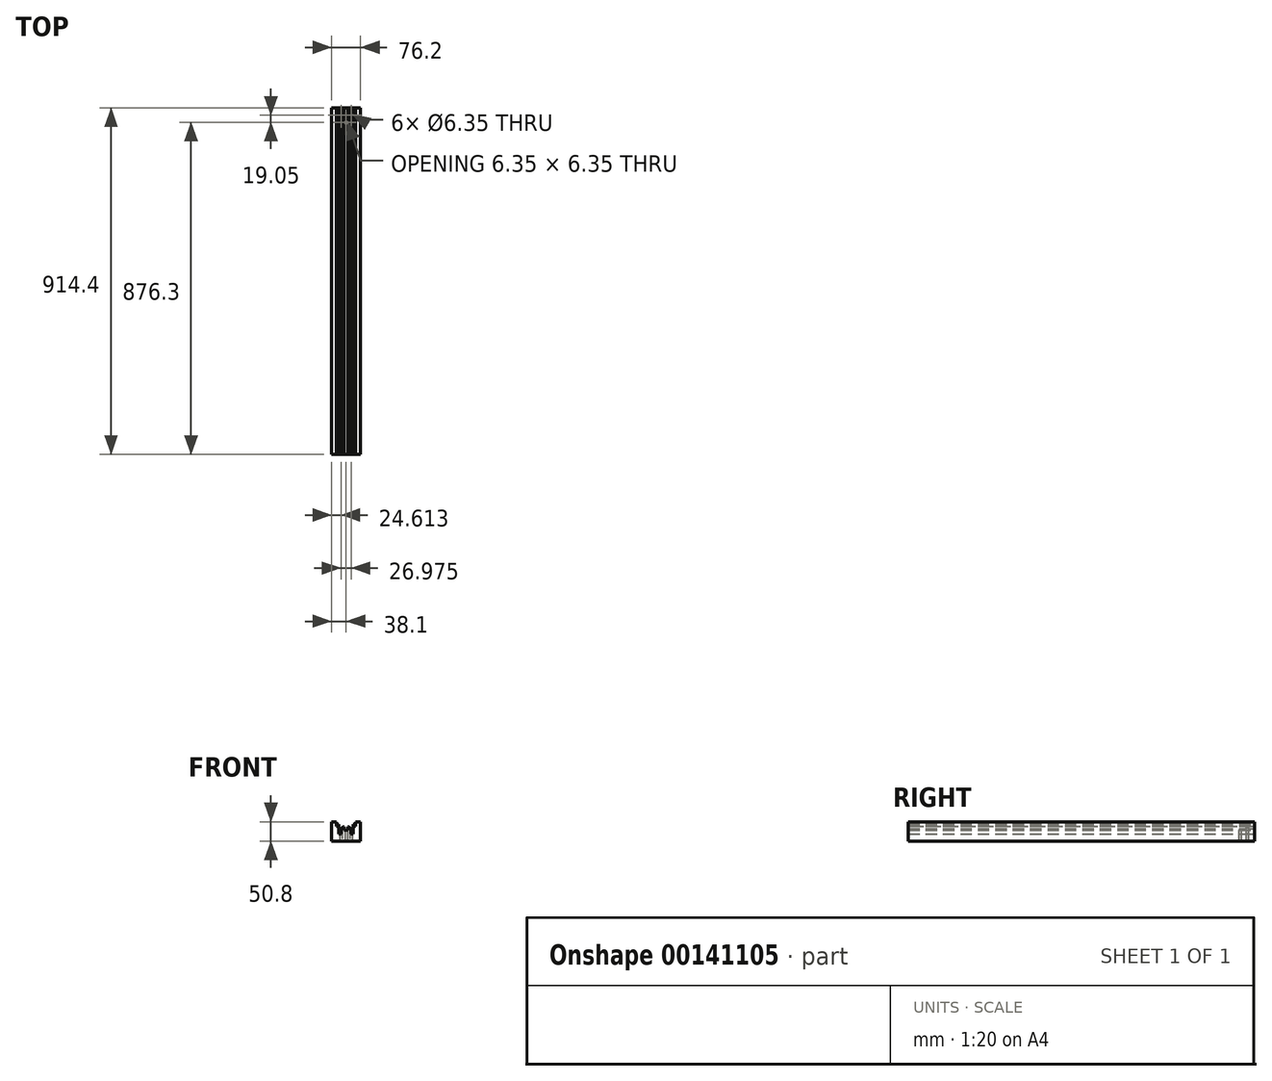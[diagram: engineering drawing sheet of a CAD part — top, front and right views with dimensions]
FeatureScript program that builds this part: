
annotation { "Feature Type Name" : "Feature", "Feature Type Description" : "" }
export const myFeature = defineFeature(function(context is Context, id is Id, definition is map)
    precondition{}
    {
        {
            var Q0;
            Q0=qCreatedBy(makeId("Front.planeOp"),FACE);
            var sketch = newSketch(context, id + "F0", { "sketchPlane" : qUnion([Q0])});
            skLineSegment(sketch, "E0.bottom", {"start": v(-38.1, 0) * mm, "end": v(38.1, 0) * mm});
            skLineSegment(sketch, "E0.top", {"start": v(-38.1, -50.8) * mm, "end": v(38.1, -50.8) * mm});
            skLineSegment(sketch, "E0.left", {"start": v(-38.1, 0) * mm, "end": v(-38.1, -50.8) * mm});
            skLineSegment(sketch, "E0.right", {"start": v(38.1, 0) * mm, "end": v(38.1, -50.8) * mm});
            skSolve(sketch);
        }
        {
            var Q0;
            Q0 = qSketchRegion(id + "F0", true);
            extrude(context, id + "F1", {"entities" : qUnion([Q0]), "depth" : 914.4 * mm});
        }
        {
            var Q0;
            Q0=qCreatedBy(makeId("Front.planeOp"),FACE);
            var sketch = newSketch(context, id + "F2", { "sketchPlane" : qUnion([Q0])});
            skLineSegment(sketch, "E1.bottom", {"start": v(-25.4, 0) * mm, "end": v(25.4, 0) * mm});
            skLineSegment(sketch, "E1.top", {"start": v(-25.4, -6.35) * mm, "end": v(25.4, -6.35) * mm});
            skLineSegment(sketch, "E1.left", {"start": v(-25.4, 0) * mm, "end": v(-25.4, -6.35) * mm});
            skLineSegment(sketch, "E1.right", {"start": v(25.4, 0) * mm, "end": v(25.4, -6.35) * mm});
            skSolve(sketch);
        }
        {
            var Q0;
            Q0 = qSketchRegion(id + "F2", true);
            extrude(context, id + "F3", {"entities" : qUnion([Q0]), "operationType" : NewBodyOperationType.REMOVE, "endBound" : BoundingType.THROUGH_ALL, "depth" : 25.4 * mm});
        }
        {
            var Q0;
            Q0=qCreatedBy(makeId("Front.planeOp"),FACE);
            var sketch = newSketch(context, id + "F4", { "sketchPlane" : qUnion([Q0])});
            skLineSegment(sketch, "E2", {"start": v(0, 0) * mm, "end": v(0, -46.04) * mm, "construction": true});
            skLineSegment(sketch, "E3", {"start": v(-19.05, -6.35) * mm, "end": v(-19.05, -31.75) * mm});
            skLineSegment(sketch, "E4", {"start": v(-19.05, -31.75) * mm, "end": v(-12.7, -31.75) * mm});
            skLineSegment(sketch, "E5", {"start": v(-12.7, -31.75) * mm, "end": v(-12.7, -12.7) * mm});
            skLineSegment(sketch, "E6", {"start": v(-12.7, -12.7) * mm, "end": v(-4.76, -12.7) * mm});
            skLineSegment(sketch, "E7", {"start": v(-4.76, -12.7) * mm, "end": v(-4.76, -22.23) * mm});
            skLineSegment(sketch, "E8", {"start": v(-4.76, -22.23) * mm, "end": v(0, -22.23) * mm});
            skLineSegment(sketch, "E9", {"start": v(-19.05, -6.35) * mm, "end": v(0, -6.35) * mm});
            skLineSegment(sketch, "E10.MirrorCS", {"start": v(4.76, -22.23) * mm, "end": v(0, -22.23) * mm});
            skLineSegment(sketch, "E11.MirrorCS", {"start": v(19.05, -6.35) * mm, "end": v(0, -6.35) * mm});
            skLineSegment(sketch, "E12.MirrorCS", {"start": v(4.76, -12.7) * mm, "end": v(4.76, -22.23) * mm});
            skLineSegment(sketch, "E13.MirrorCS", {"start": v(12.7, -12.7) * mm, "end": v(4.76, -12.7) * mm});
            skLineSegment(sketch, "E14.MirrorCS", {"start": v(19.05, -6.35) * mm, "end": v(19.05, -31.75) * mm});
            skLineSegment(sketch, "E15.MirrorCS", {"start": v(19.05, -31.75) * mm, "end": v(12.7, -31.75) * mm});
            skLineSegment(sketch, "E16.MirrorCS", {"start": v(12.7, -31.75) * mm, "end": v(12.7, -12.7) * mm});
            skSolve(sketch);
        }
        {
            var Q0;
            Q0 = qSketchRegion(id + "F4", true);
            extrude(context, id + "F5", {"entities" : qUnion([Q0]), "operationType" : NewBodyOperationType.REMOVE, "endBound" : BoundingType.THROUGH_ALL, "depth" : 25.4 * mm});
        }
        {
            var Q0;
            Q0=qCreatedBy(makeId("Front.planeOp"),FACE);
            var sketch = newSketch(context, id + "F6", { "sketchPlane" : qUnion([Q0])});
            skLineSegment(sketch, "E17.bottom", {"start": v(-25.4, -6.35) * mm, "end": v(-22.23, -6.35) * mm});
            skLineSegment(sketch, "E17.top", {"start": v(-25.4, -11.11) * mm, "end": v(-22.23, -11.11) * mm});
            skLineSegment(sketch, "E17.left", {"start": v(-25.4, -6.35) * mm, "end": v(-25.4, -11.11) * mm});
            skLineSegment(sketch, "E17.right", {"start": v(-22.23, -6.35) * mm, "end": v(-22.23, -11.11) * mm});
            skLineSegment(sketch, "E18", {"start": v(0, 0) * mm, "end": v(0, -11.71) * mm, "construction": true});
            skLineSegment(sketch, "E19.MirrorCS", {"start": v(25.4, -6.35) * mm, "end": v(22.23, -6.35) * mm});
            skLineSegment(sketch, "E20.MirrorCS", {"start": v(22.23, -6.35) * mm, "end": v(22.23, -11.11) * mm});
            skLineSegment(sketch, "E21.MirrorCS", {"start": v(25.4, -6.35) * mm, "end": v(25.4, -11.11) * mm});
            skLineSegment(sketch, "E22.MirrorCS", {"start": v(25.4, -11.11) * mm, "end": v(22.23, -11.11) * mm});
            skSolve(sketch);
        }
        {
            var Q0;
            Q0 = qSketchRegion(id + "F6", true);
            extrude(context, id + "F7", {"entities" : qUnion([Q0]), "operationType" : NewBodyOperationType.REMOVE, "endBound" : BoundingType.THROUGH_ALL, "depth" : 25.4 * mm});
        }
        {
            var Q0;
            Q0=makeQuery(id+"F1.opExtrude","SWEPT_FACE",FACE,{"disambiguationData":[OSD([sQuery(id+"F0.wireOp",EDGE,"E0.top")])]});
            var sketch = newSketch(context, id + "F8", { "sketchPlane" : qUnion([Q0])});
            skPoint(sketch, "E23", {"position": v(0, 38.1) * mm});
            skPoint(sketch, "E24", {"position": v(-13.49, 19.05) * mm});
            skPoint(sketch, "E25", {"position": v(13.49, 19.05) * mm});
            skLineSegment(sketch, "E26", {"start": v(0, 0) * mm, "end": v(0, 58.05) * mm, "construction": true});
            skSolve(sketch);
        }
        {
            var Q0;
            Q0=sQuery(id+"F8.wireOp",VERTEX,"E23");
            var Q1;
            Q1=makeQuery(id+"F1.opExtrude","SWEPT_BODY",BODY,{"disambiguationData":[OSD([sQuery(id+"F0.wireOp",EDGE,"E0.bottom"),sQuery(id+"F0.wireOp",EDGE,"E0.top"),sQuery(id+"F0.wireOp",EDGE,"E0.left"),sQuery(id+"F0.wireOp",EDGE,"E0.right")])]});
            hole(context, id + "F9", {"style" : HoleStyle.SIMPLE, "endStyle" : HoleEndStyle.THROUGH, "holeDiameter" : 6.35 * mm, "locations" : qUnion([Q0]), "scope" : qUnion([Q1]), "isTappedThrough" : true});
        }
        {
            var Q0;
            Q0=sQuery(id+"F8.wireOp",VERTEX,"E24");
            var Q1;
            Q1=sQuery(id+"F8.wireOp",VERTEX,"E25");
            var Q2;
            Q2=makeQuery(id+"F1.opExtrude","SWEPT_BODY",BODY,{"disambiguationData":[OSD([sQuery(id+"F0.wireOp",EDGE,"E0.bottom"),sQuery(id+"F0.wireOp",EDGE,"E0.top"),sQuery(id+"F0.wireOp",EDGE,"E0.left"),sQuery(id+"F0.wireOp",EDGE,"E0.right")])]});
            hole(context, id + "F10", {"style" : HoleStyle.SIMPLE, "endStyle" : HoleEndStyle.THROUGH, "holeDiameter" : 6.35 * mm, "locations" : qUnion([Q0, Q1]), "scope" : qUnion([Q2]), "isTappedThrough" : true});
        }
        {
            var Q0;
            {var subQ0=sQuery(id+"F4.wireOp",EDGE,"E5");var subQ1=sQuery(id+"F4.wireOp",EDGE,"E6");Q0=makeQuery(id+"F10.hole-0.boolean.opBoolean","SPLIT",EDGE,{"disambiguationData":[TD([makeQuery(id+"F1.opExtrude","CAP_FACE",FACE,{"disambiguationData":[OSD([sQuery(id+"F0.wireOp",EDGE,"E0.bottom"),sQuery(id+"F0.wireOp",EDGE,"E0.top"),sQuery(id+"F0.wireOp",EDGE,"E0.left"),sQuery(id+"F0.wireOp",EDGE,"E0.right")])],"isStart":false})])],"derivedFrom":makeQuery(id+"F5.boolean.opBoolean","COPY",EDGE,{"derivedFrom":makeQuery(id+"F5.opExtrude","SWEPT_EDGE",EDGE,{"disambiguationData":[OSD([subQ0,subQ1])]})})});}
            var Q1;
            {var subQ0=sQuery(id+"F4.wireOp",EDGE,"E13.MirrorCS");var subQ1=sQuery(id+"F4.wireOp",EDGE,"E16.MirrorCS");Q1=makeQuery(id+"F10.hole-1.boolean.opBoolean","SPLIT",EDGE,{"disambiguationData":[TD([makeQuery(id+"F1.opExtrude","CAP_FACE",FACE,{"disambiguationData":[OSD([sQuery(id+"F0.wireOp",EDGE,"E0.bottom"),sQuery(id+"F0.wireOp",EDGE,"E0.top"),sQuery(id+"F0.wireOp",EDGE,"E0.left"),sQuery(id+"F0.wireOp",EDGE,"E0.right")])],"isStart":false})])],"derivedFrom":makeQuery(id+"F5.boolean.opBoolean","COPY",EDGE,{"derivedFrom":makeQuery(id+"F5.opExtrude","SWEPT_EDGE",EDGE,{"disambiguationData":[OSD([subQ0,subQ1])]})})});}
            chamfer(context, id + "F11", {"entities" : qUnion([Q0, Q1]), "width" : 4.76 * mm, "tangentPropagation" : true});
        }
    });
